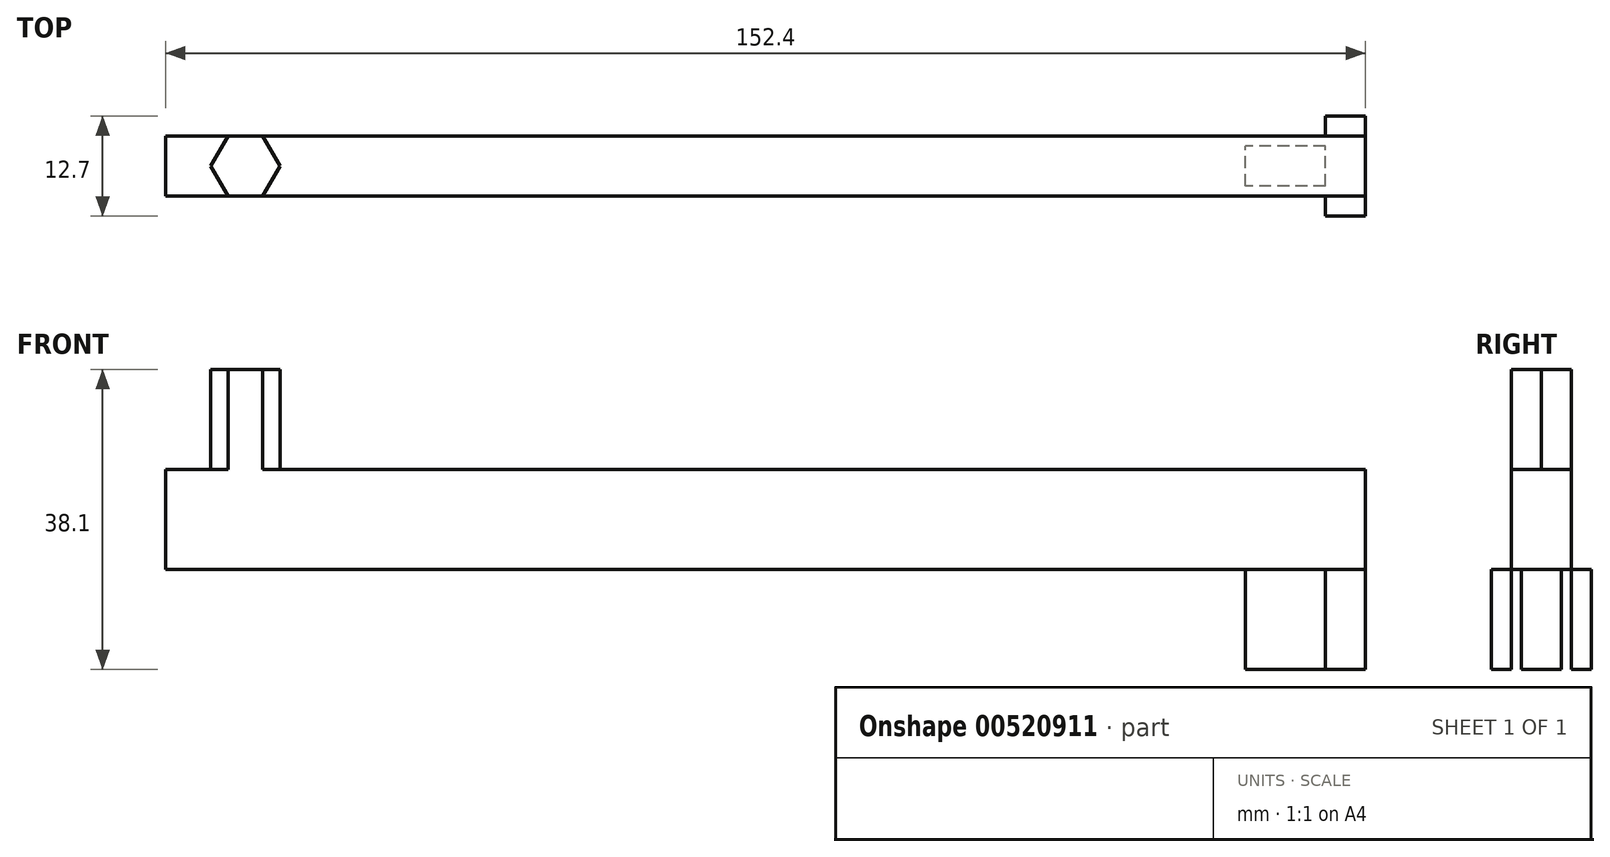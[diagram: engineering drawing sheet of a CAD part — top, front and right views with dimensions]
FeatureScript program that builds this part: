
annotation { "Feature Type Name" : "Feature", "Feature Type Description" : "" }
export const myFeature = defineFeature(function(context is Context, id is Id, definition is map)
    precondition{}
    {
        {
            var Q0;
            Q0=qCreatedBy(makeId("Top.planeOp"),FACE);
            var sketch = newSketch(context, id + "F0", { "sketchPlane" : qUnion([Q0])});
            skLineSegment(sketch, "E0.bottom", {"start": v(135.62, 3.81) * mm, "end": v(-16.78, 3.81) * mm});
            skLineSegment(sketch, "E0.top", {"start": v(135.62, -3.81) * mm, "end": v(-16.78, -3.81) * mm});
            skLineSegment(sketch, "E0.left", {"start": v(135.62, 3.81) * mm, "end": v(135.62, -3.81) * mm});
            skLineSegment(sketch, "E0.right", {"start": v(-16.78, 3.81) * mm, "end": v(-16.78, -3.81) * mm});
            skCircle(sketch, "E1.cCircle", {"center": v(-6.65, 0) * mm, "radius": 3.81 * mm, "construction": true});
            skLineSegment(sketch, "E1.0", {"start": v(-11.05, 0) * mm, "end": v(-8.85, 3.8) * mm});
            skLineSegment(sketch, "E1.1", {"start": v(-8.85, 3.8) * mm, "end": v(-4.45, 3.81) * mm});
            skLineSegment(sketch, "E1.2", {"start": v(-4.45, 3.81) * mm, "end": v(-2.25, 0) * mm});
            skLineSegment(sketch, "E1.3", {"start": v(-2.25, 0) * mm, "end": v(-4.44, -3.8) * mm});
            skLineSegment(sketch, "E1.4", {"start": v(-4.44, -3.8) * mm, "end": v(-8.84, -3.81) * mm});
            skLineSegment(sketch, "E1.5", {"start": v(-8.84, -3.81) * mm, "end": v(-11.05, 0) * mm});
            skPoint(sketch, "E1.0.midPoint", {"position": v(-9.95, 1.9) * mm});
            skSolve(sketch);
        }
        {
            var Q0;
            Q0=makeQuery(id+"F0.imprint","IMPRINT",FACE,{"disambiguationData":[TD([[makeQuery(id+"F0.imprint","IMPRINT",EDGE,{"derivedFrom":sQuery(id+"F0.wireOp",EDGE,"E0.bottom")}),1.0]])]});
            var Q1;
            Q1=makeQuery(id+"F0.imprint","IMPRINT",FACE,{"disambiguationData":[TD([[makeQuery(id+"F0.imprint","IMPRINT",EDGE,{"derivedFrom":sQuery(id+"F0.wireOp",EDGE,"c2bde3be-c9e3-41ed-898e-f052cf146410.0")}),-1.0]])]});
            var Q2;
            Q2=makeQuery(id+"F0.imprint","IMPRINT",FACE,{"disambiguationData":[TD([[makeQuery(id+"F0.imprint","IMPRINT",EDGE,{"derivedFrom":sQuery(id+"F0.wireOp",EDGE,"E1.0")}),-1.0]])]});
            extrude(context, id + "F1", {"entities" : qUnion([Q0, Q1, Q2]), "oppositeDirection" : true, "depth" : 12.7 * mm, "offsetDistance" : 25.4 * mm});
        }
        {
            var Q0;
            Q0=makeQuery(id+"F1.opExtrude","CAP_FACE",FACE,{"disambiguationData":[OSD([sQuery(id+"F0.wireOp",EDGE,"E0.bottom"),sQuery(id+"F0.wireOp",EDGE,"E0.top"),sQuery(id+"F0.wireOp",EDGE,"E0.left"),sQuery(id+"F0.wireOp",EDGE,"E0.right")])],"isStart":false});
            var sketch = newSketch(context, id + "F2", { "sketchPlane" : qUnion([Q0])});
            skLineSegment(sketch, "E2.bottom", {"start": v(130.54, 6.35) * mm, "end": v(135.62, 6.35) * mm});
            skLineSegment(sketch, "E2.top", {"start": v(130.54, -6.35) * mm, "end": v(135.62, -6.35) * mm});
            skLineSegment(sketch, "E2.left", {"start": v(130.54, 6.35) * mm, "end": v(130.54, -6.35) * mm});
            skLineSegment(sketch, "E2.right", {"start": v(135.62, 6.35) * mm, "end": v(135.62, -6.35) * mm});
            skLineSegment(sketch, "E3.left", {"start": v(130.54, 2.54) * mm, "end": v(130.54, -2.54) * mm});
            skLineSegment(sketch, "E4.bottom", {"start": v(130.54, 2.54) * mm, "end": v(120.38, 2.54) * mm});
            skLineSegment(sketch, "E4.top", {"start": v(130.54, -2.54) * mm, "end": v(120.38, -2.54) * mm});
            skLineSegment(sketch, "E4.right", {"start": v(120.38, 2.54) * mm, "end": v(120.38, -2.54) * mm});
            skSolve(sketch);
        }
        {
            var Q0;
            {var subQ0=sQuery(id+"F2.wireOp",EDGE,"E2.bottom");Q0=makeQuery(id+"F2.imprint","IMPRINT",FACE,{"disambiguationData":[TD([[makeQuery(id+"F2.imprint","IMPRINT",EDGE,{"derivedFrom":subQ0}),-1.0]])]});}
            var Q1;
            {var subQ0=sQuery(id+"F2.wireOp",EDGE,"E3.left");Q1=makeQuery(id+"F2.imprint","IMPRINT",FACE,{"disambiguationData":[TD([[makeQuery(id+"F2.imprint","IMPRINT",EDGE,{"derivedFrom":subQ0}),1.0]])]});}
            var Q2;
            {var subQ0=sQuery(id+"F2.wireOp",EDGE,"E2.top");Q2=makeQuery(id+"F2.imprint","IMPRINT",FACE,{"disambiguationData":[TD([[makeQuery(id+"F2.imprint","IMPRINT",EDGE,{"derivedFrom":subQ0}),1.0]])]});}
            var Q3;
            Q3=makeQuery(id+"F2.imprint","IMPRINT",FACE,{"disambiguationData":[TD([[makeQuery(id+"F2.imprint","IMPRINT",EDGE,{"derivedFrom":sQuery(id+"F2.wireOp",EDGE,"E4.bottom")}),1.0]])]});
            extrude(context, id + "F3", {"entities" : qUnion([Q0, Q1, Q2, Q3]), "operationType" : NewBodyOperationType.ADD, "depth" : 12.7 * mm, "offsetDistance" : 25.4 * mm});
        }
        {
            var Q0;
            Q0=makeQuery(id+"F0.imprint","IMPRINT",FACE,{"disambiguationData":[TD([[makeQuery(id+"F0.imprint","IMPRINT",EDGE,{"derivedFrom":sQuery(id+"F0.wireOp",EDGE,"E1.0")}),-1.0]])]});
            extrude(context, id + "F4", {"entities" : qUnion([Q0]), "operationType" : NewBodyOperationType.ADD, "depth" : 12.7 * mm, "offsetDistance" : 25.4 * mm});
        }
    });
